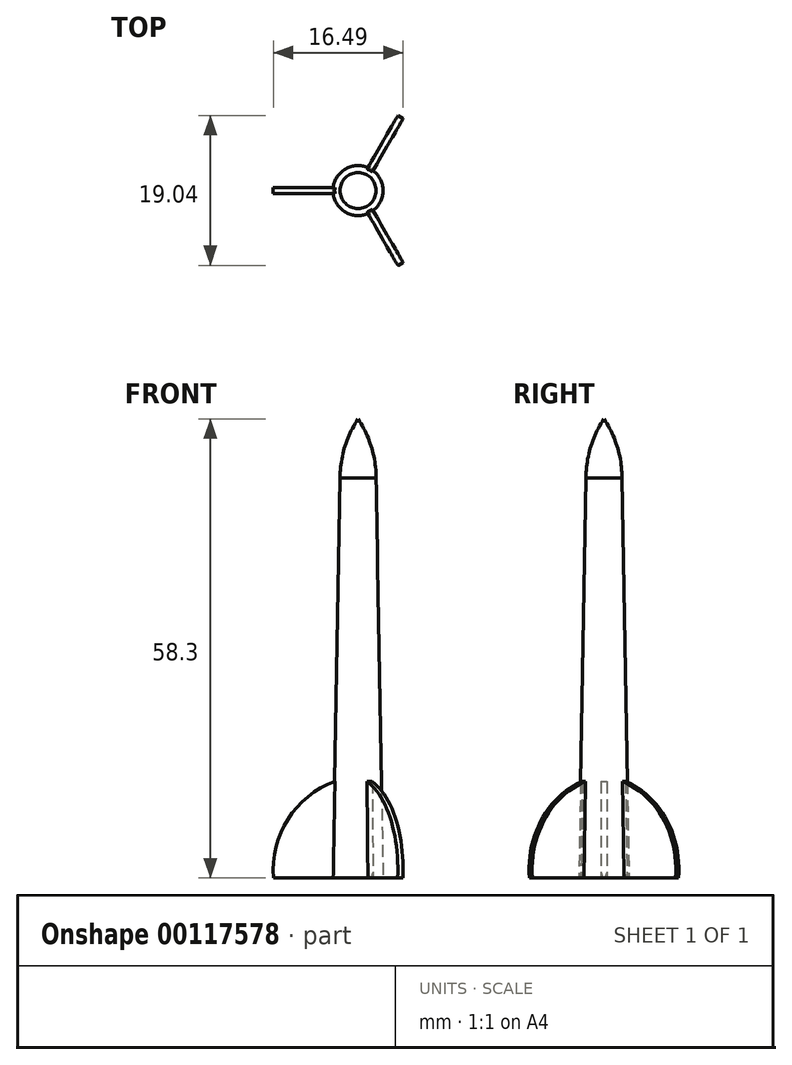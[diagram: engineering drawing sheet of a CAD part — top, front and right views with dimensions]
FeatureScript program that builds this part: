
annotation { "Feature Type Name" : "Feature", "Feature Type Description" : "" }
export const myFeature = defineFeature(function(context is Context, id is Id, definition is map)
    precondition{}
    {
        {
            var Q0;
            Q0=qCreatedBy(makeId("Top.planeOp"),FACE);
            var sketch = newSketch(context, id + "F0", { "sketchPlane" : qUnion([Q0])});
            skCircle(sketch, "E0", {"center": v(0, 0) * mm, "radius": 3.18 * mm});
            skSolve(sketch);
        }
        {
            var Q0;
            Q0=qSketchRegion(id+"F0",true);
            extrude(context, id + "F1", {"entities" : qUnion([Q0]), "depth" : 50.8 * mm, "hasDraft" : true, "draftAngle" : 1 * degree, "draftPullDirection" : true});
        }
        {
            var Q0;
            Q0=qCreatedBy(makeId("Front.planeOp"),FACE);
            var sketch = newSketch(context, id + "F2", { "sketchPlane" : qUnion([Q0])});
            skArc(sketch, "E1", {"start": v(2.29, 50.8) * mm, "mid": v(1.7, 54.72) * mm, "end": v(0, 58.3) * mm});
            skLineSegment(sketch, "E2", {"start": v(0, 58.3) * mm, "end": v(0, 50.8) * mm});
            skLineSegment(sketch, "E3", {"start": v(0, 50.8) * mm, "end": v(2.29, 50.8) * mm});
            skSolve(sketch);
        }
        {
            var Q0;
            Q0=qSketchRegion(id+"F2",true);
            var Q1;
            Q1=sQuery(id+"F2.wireOp",EDGE,"E2");
            revolve(context, id + "F3", {"operationType" : NewBodyOperationType.ADD, "entities" : qUnion([Q0]), "axis" : qUnion([Q1]), "revolveType" : RevolveType.FULL});
        }
        {
            var Q0;
            Q0=qCreatedBy(makeId("Front.planeOp"),FACE);
            var sketch = newSketch(context, id + "F4", { "sketchPlane" : qUnion([Q0])});
            skArc(sketch, "E4", {"start": v(-3.18, 0) * mm, "mid": v(-6.57, -2.04) * mm, "end": v(-9.02, -5.16) * mm, "construction": true});
            skArc(sketch, "E5", {"start": v(-2.52, 12.4) * mm, "mid": v(-8.8, 7.63) * mm, "end": v(-10.73, 0) * mm});
            skLineSegment(sketch, "E6", {"start": v(-2.52, 12.4) * mm, "end": v(-3.17, 0) * mm});
            skLineSegment(sketch, "E7", {"start": v(-3.18, 0) * mm, "end": v(-10.73, 0) * mm});
            skSolve(sketch);
        }
        {
            var Q0;
            Q0=qSketchRegion(id+"F4",true);
            extrude(context, id + "F5", {"entities" : qUnion([Q0]), "depth" : 0.76 * mm, "symmetric" : true});
        }
        {
            var Q0;
            Q0=makeQuery(id+"F5.opExtrude","SWEPT_BODY",BODY,{"disambiguationData":[OSD([sQuery(id+"F4.wireOp",EDGE,"E4"),sQuery(id+"F4.wireOp",EDGE,"E5"),sQuery(id+"F4.wireOp",EDGE,"E6")])]});
            var Q1;
            Q1=makeQuery(id+"F1.opExtrude","SWEPT_FACE",FACE,{"disambiguationData":[OSD([sQuery(id+"F0.wireOp",EDGE,"E0")])]});
            circularPattern(context, id + "F6", {"operationType" : NewBodyOperationType.ADD, "entities" : qUnion([Q0]), "axis" : qUnion([Q1]), "angle" : 360 * degree, "instanceCount" : round(3), "equalSpace" : true, "computeTransformsWithoutBuiltin" : true});
        }
    });
